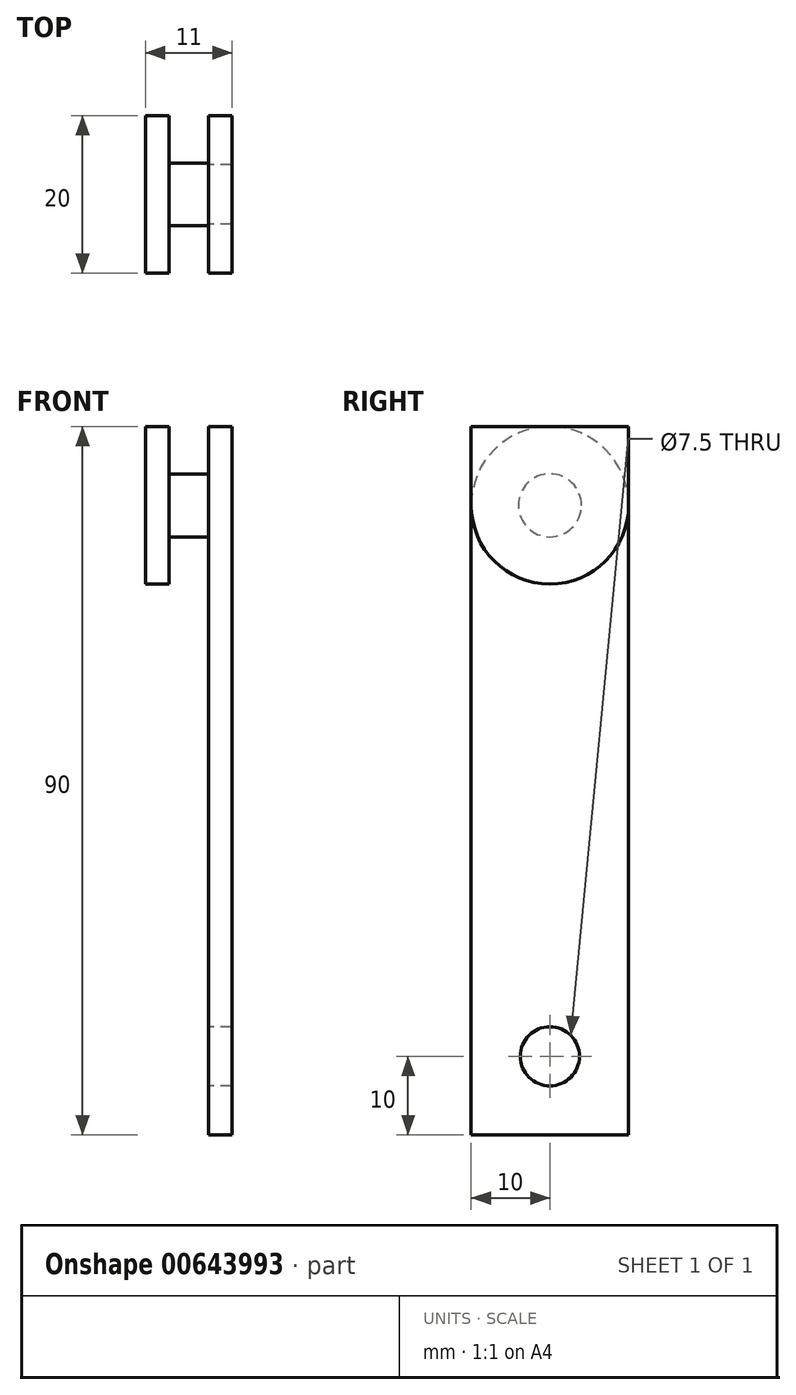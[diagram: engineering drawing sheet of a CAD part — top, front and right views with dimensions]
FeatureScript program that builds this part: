
annotation { "Feature Type Name" : "Feature", "Feature Type Description" : "" }
export const myFeature = defineFeature(function(context is Context, id is Id, definition is map)
    precondition{}
    {
        {
            var Q0;
            Q0=qCreatedBy(makeId("Right.planeOp"),FACE);
            var sketch = newSketch(context, id + "F0", { "sketchPlane" : qUnion([Q0])});
            skLineSegment(sketch, "E0", {"start": v(0, 0) * mm, "end": v(0, 90) * mm});
            skLineSegment(sketch, "E1", {"start": v(0, 90) * mm, "end": v(20, 90) * mm});
            skLineSegment(sketch, "E2", {"start": v(20, 90) * mm, "end": v(20, 0) * mm});
            skLineSegment(sketch, "E3", {"start": v(20, 0) * mm, "end": v(0, 0) * mm});
            skCircle(sketch, "E4", {"center": v(10, 80) * mm, "radius": 4 * mm});
            skPoint(sketch, "E4.centerSnap0", {"position": v(10, 90) * mm});
            skCircle(sketch, "E5", {"center": v(10, 10) * mm, "radius": 3.75 * mm});
            skPoint(sketch, "E5.centerSnap0", {"position": v(10, 0) * mm});
            skSolve(sketch);
        }
        {
            var Q0;
            Q0=makeQuery(id+"F0.imprint","IMPRINT",FACE,{"disambiguationData":[TD([[makeQuery(id+"F0.imprint","IMPRINT",EDGE,{"derivedFrom":sQuery(id+"F0.wireOp",EDGE,"E0")}),-1.0]])]});
            var Q1;
            Q1=makeQuery(id+"F0.imprint","IMPRINT",FACE,{"disambiguationData":[TD([[makeQuery(id+"F0.imprint","IMPRINT",EDGE,{"derivedFrom":sQuery(id+"F0.wireOp",EDGE,"E4")}),1.0]])]});
            extrude(context, id + "F1", {"entities" : qUnion([Q0, Q1]), "depth" : 3 * mm, "offsetDistance" : 25 * mm});
        }
        {
            var Q0;
            Q0=makeQuery(id+"F0.imprint","IMPRINT",FACE,{"disambiguationData":[TD([[makeQuery(id+"F0.imprint","IMPRINT",EDGE,{"derivedFrom":sQuery(id+"F0.wireOp",EDGE,"E4")}),1.0]])]});
            extrude(context, id + "F2", {"entities" : qUnion([Q0]), "operationType" : NewBodyOperationType.ADD, "oppositeDirection" : true, "depth" : 5 * mm, "offsetDistance" : 25 * mm});
        }
        {
            var Q0;
            Q0=qCreatedBy(makeId("Right.planeOp"),FACE);
            cPlane(context, id + "F3", {"entities" : qUnion([Q0]), "cplaneType" : CPlaneType.OFFSET, "offset" : 5 * mm, "oppositeDirection" : true, "width" : 150 * mm, "height" : 150 * mm});
        }
        {
            var Q0;
            Q0=qCreatedBy(id+"F3.planeOp",FACE);
            var sketch = newSketch(context, id + "F4", { "sketchPlane" : qUnion([Q0])});
            skPoint(sketch, "E6", {"position": v(10, 80) * mm});
            skCircle(sketch, "E7", {"center": v(10, 80) * mm, "radius": 10 * mm});
            skSolve(sketch);
        }
        {
            var Q0;
            Q0 = qSketchRegion(id + "F4", true);
            extrude(context, id + "F5", {"entities" : qUnion([Q0]), "operationType" : NewBodyOperationType.ADD, "oppositeDirection" : true, "depth" : 3 * mm, "offsetDistance" : 25 * mm});
        }
    });
